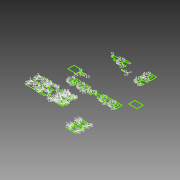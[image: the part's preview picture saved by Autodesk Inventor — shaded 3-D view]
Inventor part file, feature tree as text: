
AUTODESK INVENTOR PART (.ipt)
format: ipt  version: 2012 (Build 160160000, 160)  size: 239,616 bytes
history: native  units: mm
features: sketch x1
ambient origin geometry x8: Origin, YZ Plane, XZ Plane, XY Plane, X Axis, Y Axis, Z Axis, Center Point
feature tree (1):
  sketch  "Sketch1"  dims[d0=5.0mm d1=5.0mm d2=50.0mm d3=41.0mm d4=5.0mm d5=5.0mm d6=5.0mm d7=50.0mm d8=41.0mm d9=2.0mm d10=41.0mm d11=5.0mm d12=5.0mm d13=5.0mm d14=50.0mm d15=41.0mm d16=5.0mm d17=5.0mm d18=50.0mm d19=41.0mm d20=5.0mm d21=5.0mm d22=5.0mm d23=50.0mm d24=41.0mm d25=5.0mm d26=5.0mm d27=5.0mm d28=50.0mm d29=41.0mm d30=5.0mm d31=5.0mm d32=50.0mm d33=41.0mm d35=15.0mm d36=29.996525mm d41=21.0mm d42=15.0mm d43=29.996525mm d44=35.0mm d53=21.0mm d54=20.0mm d55=35.0mm d57=2.0mm d58=10.0mm d59=43.0mm d60=10.0mm d61=14.0mm d62=14.0mm d71=40.0mm d72=23.0mm d73=2.0mm d74=10.0mm d75=50.0mm d76=43.0mm d77=60.0mm d78=43.0mm d88=3.0mm d89=21.5mm d91=5.0mm d92=3.0mm d93=5.0mm d94=21.5mm d95=60.0mm d96=43.0mm d97=3.0mm d98=21.5mm d99=5.0mm d100=3.0mm d101=5.0mm d102=21.5mm d103=3.0mm d104=5.0mm d105=21.5mm d106=40.0mm d107=23.0mm d108=2.0mm d109=10.0mm d110=50.0mm d111=43.0mm d112=3.0mm d113=5.0mm d114=21.5mm d118=3.0mm d119=5.0mm d120=21.5mm d126=3.0mm d127=5.0mm d128=21.5mm d129=3.0mm d130=5.0mm d131=21.5mm d132=35.0mm d133=2.0mm d134=10.0mm d135=43.0mm d136=10.0mm d137=14.0mm d138=14.0mm d139=3.0mm d140=5.0mm d141=21.5mm d142=2.0mm d143=43.0mm d144=3.0mm d145=5.0mm d146=21.5mm d147=3.0mm d148=5.0mm d149=21.5mm d150=2.0mm d151=43.0mm d152=3.0mm d153=5.0mm d154=21.5mm d155=3.0mm d156=5.0mm d157=21.5mm d158=40.0mm d159=23.0mm d160=2.0mm d161=10.0mm d162=50.0mm d163=43.0mm d164=3.0mm d165=5.0mm d166=21.5mm d167=40.0mm d168=23.0mm d169=2.0mm d170=10.0mm d171=50.0mm d172=43.0mm d173=3.0mm d174=5.0mm d175=21.5mm]
